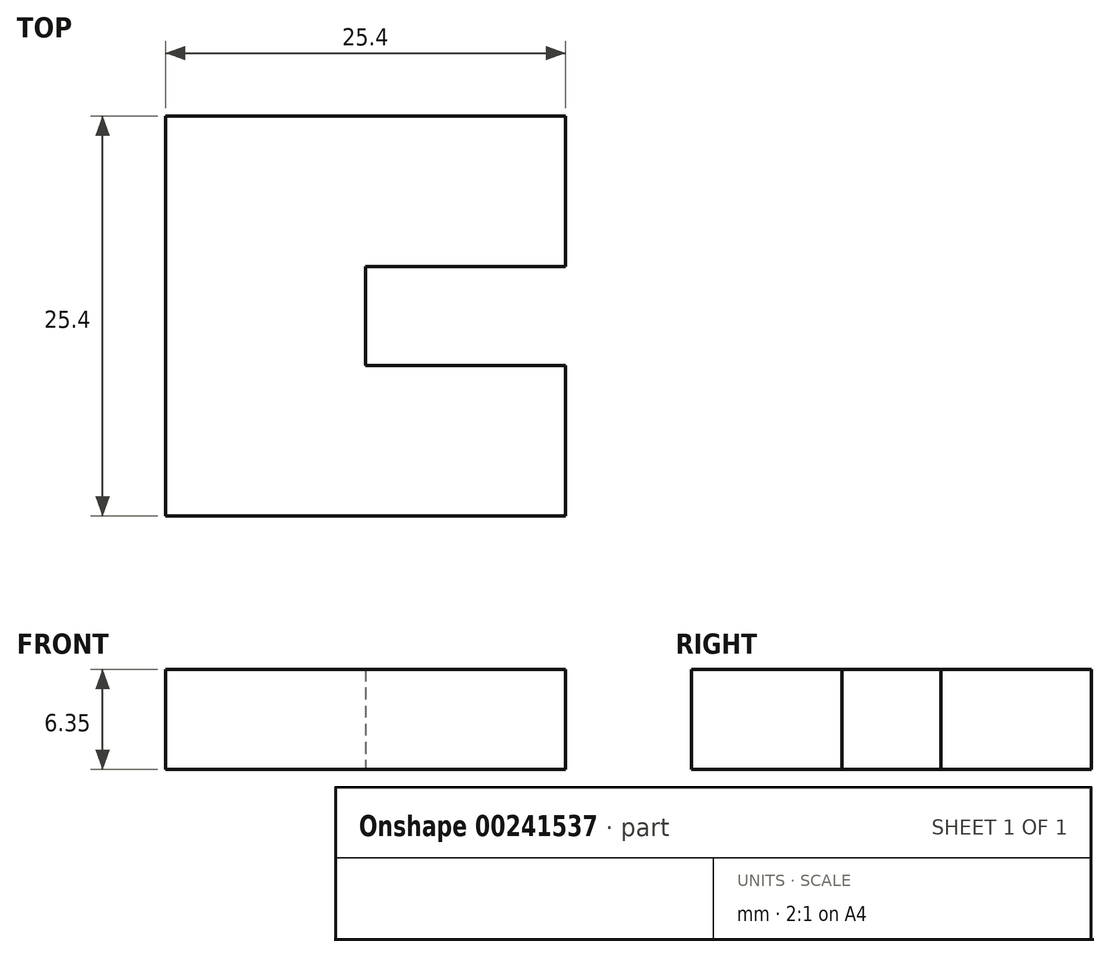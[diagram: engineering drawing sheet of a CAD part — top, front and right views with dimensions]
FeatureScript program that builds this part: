
annotation { "Feature Type Name" : "Feature", "Feature Type Description" : "" }
export const myFeature = defineFeature(function(context is Context, id is Id, definition is map)
    precondition{}
    {
        {
            var Q0;
            Q0=qCreatedBy(makeId("Top.planeOp"),FACE);
            var sketch = newSketch(context, id + "F0", { "sketchPlane" : qUnion([Q0])});
            skLineSegment(sketch, "E0", {"start": v(0, 0) * mm, "end": v(0, 25.4) * mm});
            skLineSegment(sketch, "E1", {"start": v(0, 25.4) * mm, "end": v(25.4, 25.4) * mm});
            skLineSegment(sketch, "E2", {"start": v(25.4, 25.4) * mm, "end": v(25.4, 15.84) * mm});
            skLineSegment(sketch, "E3", {"start": v(25.4, 15.84) * mm, "end": v(12.7, 15.84) * mm});
            skLineSegment(sketch, "E4", {"start": v(12.7, 15.84) * mm, "end": v(12.7, 9.56) * mm});
            skLineSegment(sketch, "E5", {"start": v(12.7, 9.56) * mm, "end": v(25.4, 9.56) * mm});
            skLineSegment(sketch, "E6", {"start": v(25.4, 9.56) * mm, "end": v(25.4, 0) * mm});
            skLineSegment(sketch, "E7", {"start": v(25.4, 0) * mm, "end": v(0, 0) * mm});
            skSolve(sketch);
        }
        {
            var Q0;
            Q0=makeQuery(id+"F0.imprint","IMPRINT",FACE,{"disambiguationData":[TD([[makeQuery(id+"F0.imprint","IMPRINT",EDGE,{"derivedFrom":sQuery(id+"F0.wireOp",EDGE,"E0")}),-1.0]])]});
            extrude(context, id + "F1", {"entities" : qUnion([Q0]), "depth" : 6.35 * mm});
        }
    });
